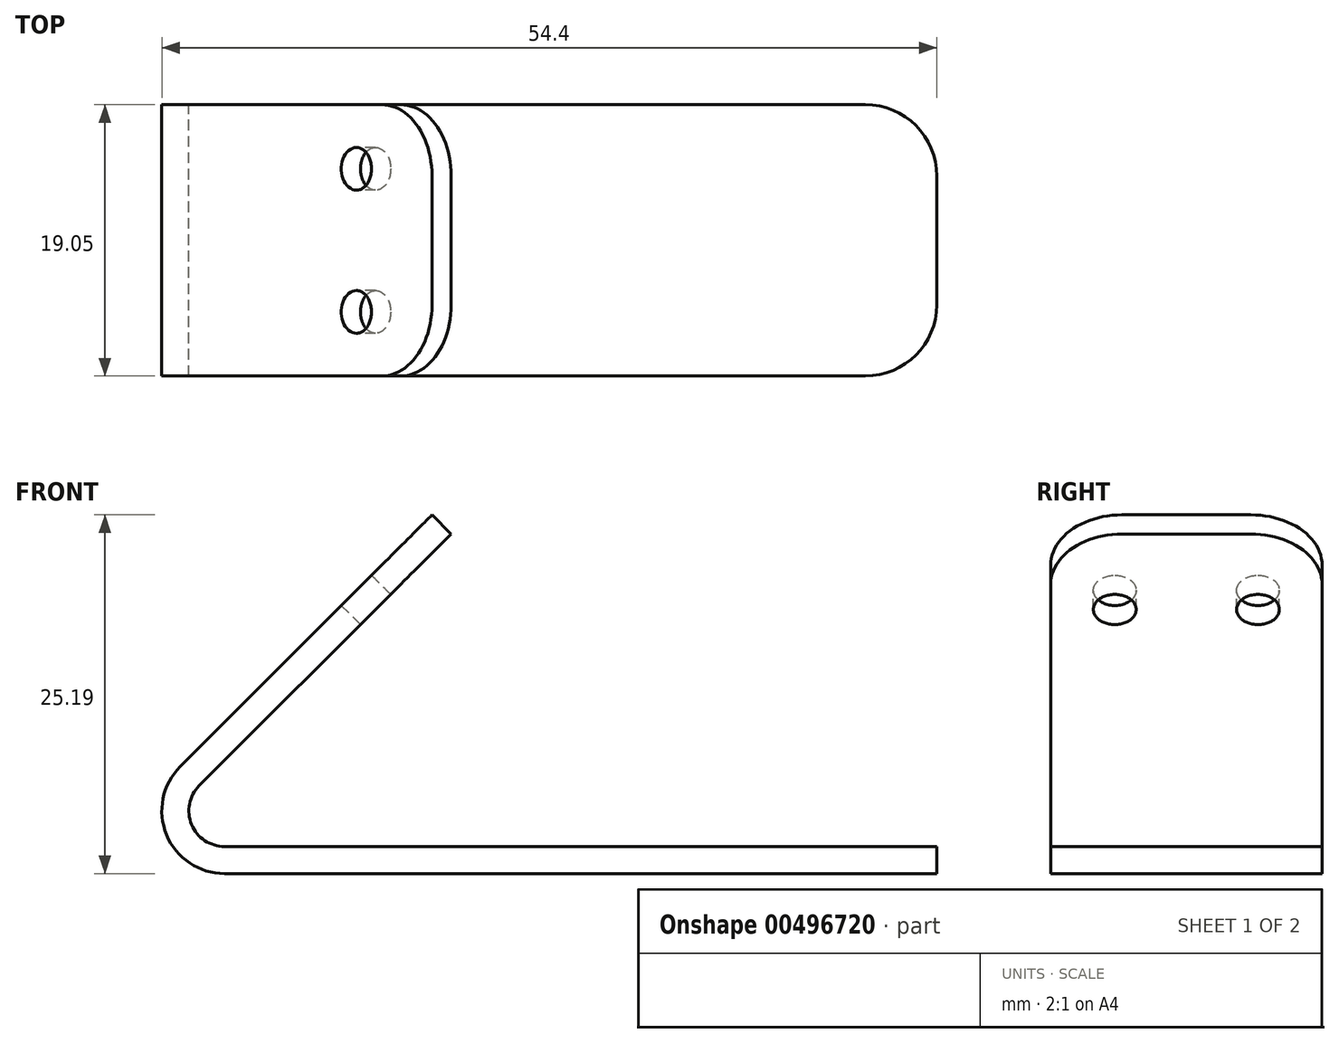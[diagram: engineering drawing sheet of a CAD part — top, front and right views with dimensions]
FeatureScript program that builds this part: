
annotation { "Feature Type Name" : "Feature", "Feature Type Description" : "" }
export const myFeature = defineFeature(function(context is Context, id is Id, definition is map)
    precondition{}
    {
        {
            var Q0;
            Q0=qCreatedBy(makeId("Front.planeOp"),FACE);
            var sketch = newSketch(context, id + "F0", { "sketchPlane" : qUnion([Q0])});
            skLineSegment(sketch, "E0", {"start": v(2, 32.46) * mm, "end": v(-15.67, 14.78) * mm});
            skLineSegment(sketch, "E1", {"start": v(-12.56, 7.27) * mm, "end": v(37.44, 7.27) * mm});
            skPoint(sketch, "E2.visualSharp", {"position": v(-23.19, 7.27) * mm});
            skArc(sketch, "E2.filletArc", {"start": v(-15.67, 14.78) * mm, "mid": v(-16.63, 9.99) * mm, "end": v(-12.56, 7.27) * mm});
            skLineSegment(sketch, "E3.0", {"start": v(-12.56, 9.17) * mm, "end": v(37.44, 9.17) * mm});
            skArc(sketch, "E3.1", {"start": v(-14.33, 13.44) * mm, "mid": v(-14.87, 10.72) * mm, "end": v(-12.56, 9.17) * mm});
            skLineSegment(sketch, "E3.2", {"start": v(3.35, 31.12) * mm, "end": v(-14.33, 13.44) * mm});
            skLineSegment(sketch, "E4", {"start": v(2, 32.46) * mm, "end": v(3.35, 31.12) * mm});
            skLineSegment(sketch, "E5", {"start": v(37.44, 9.17) * mm, "end": v(37.44, 7.27) * mm});
            skSolve(sketch);
        }
        {
            var Q0;
            Q0=makeQuery(id+"F0.imprint","IMPRINT",FACE,{"disambiguationData":[TD([[makeQuery(id+"F0.imprint","IMPRINT",EDGE,{"derivedFrom":sQuery(id+"F0.wireOp",EDGE,"E0")}),1.0]])]});
            extrude(context, id + "F1", {"entities" : qUnion([Q0]), "depth" : 19.05 * mm});
        }
        {
            var Q0;
            Q0=makeQuery(id+"F1.opExtrude","CAP_EDGE",EDGE,{"disambiguationData":[OSD([sQuery(id+"F0.wireOp",EDGE,"E5")])],"isStart":false});
            var Q1;
            Q1=makeQuery(id+"F1.opExtrude","CAP_EDGE",EDGE,{"disambiguationData":[OSD([sQuery(id+"F0.wireOp",EDGE,"E5")])],"isStart":true});
            var Q2;
            Q2=makeQuery(id+"F1.opExtrude","CAP_EDGE",EDGE,{"disambiguationData":[OSD([sQuery(id+"F0.wireOp",EDGE,"E4")])],"isStart":false});
            var Q3;
            Q3=makeQuery(id+"F1.opExtrude","CAP_EDGE",EDGE,{"disambiguationData":[OSD([sQuery(id+"F0.wireOp",EDGE,"E4")])],"isStart":true});
            fillet(context, id + "F2", {"entities" : qUnion([Q0, Q1, Q2, Q3]), "radius" : 5 * mm, "tangentPropagation" : true, "allowEdgeOverflow" : false});
        }
        {
            var Q0;
            Q0=makeQuery(id+"F1.opExtrude","SWEPT_FACE",FACE,{"disambiguationData":[OSD([sQuery(id+"F0.wireOp",EDGE,"E0")])]});
            var sketch = newSketch(context, id + "F3", { "sketchPlane" : qUnion([Q0])});
            skCircle(sketch, "E6", {"center": v(14.55, 16.87) * mm, "radius": 1.5 * mm});
            skCircle(sketch, "E7", {"center": v(4.5, 16.87) * mm, "radius": 1.5 * mm});
            skSolve(sketch);
        }
        {
            var Q0;
            Q0=makeQuery(id+"F3.imprint","IMPRINT",FACE,{"disambiguationData":[TD([[makeQuery(id+"F3.imprint","IMPRINT",EDGE,{"derivedFrom":sQuery(id+"F3.wireOp",EDGE,"E7")}),1.0]])]});
            var Q1;
            Q1=makeQuery(id+"F3.imprint","IMPRINT",FACE,{"disambiguationData":[TD([[makeQuery(id+"F3.imprint","IMPRINT",EDGE,{"derivedFrom":sQuery(id+"F3.wireOp",EDGE,"E6")}),1.0]])]});
            extrude(context, id + "F4", {"entities" : qUnion([Q0, Q1]), "operationType" : NewBodyOperationType.REMOVE, "oppositeDirection" : true, "depth" : 2.6 * mm});
        }
    });
